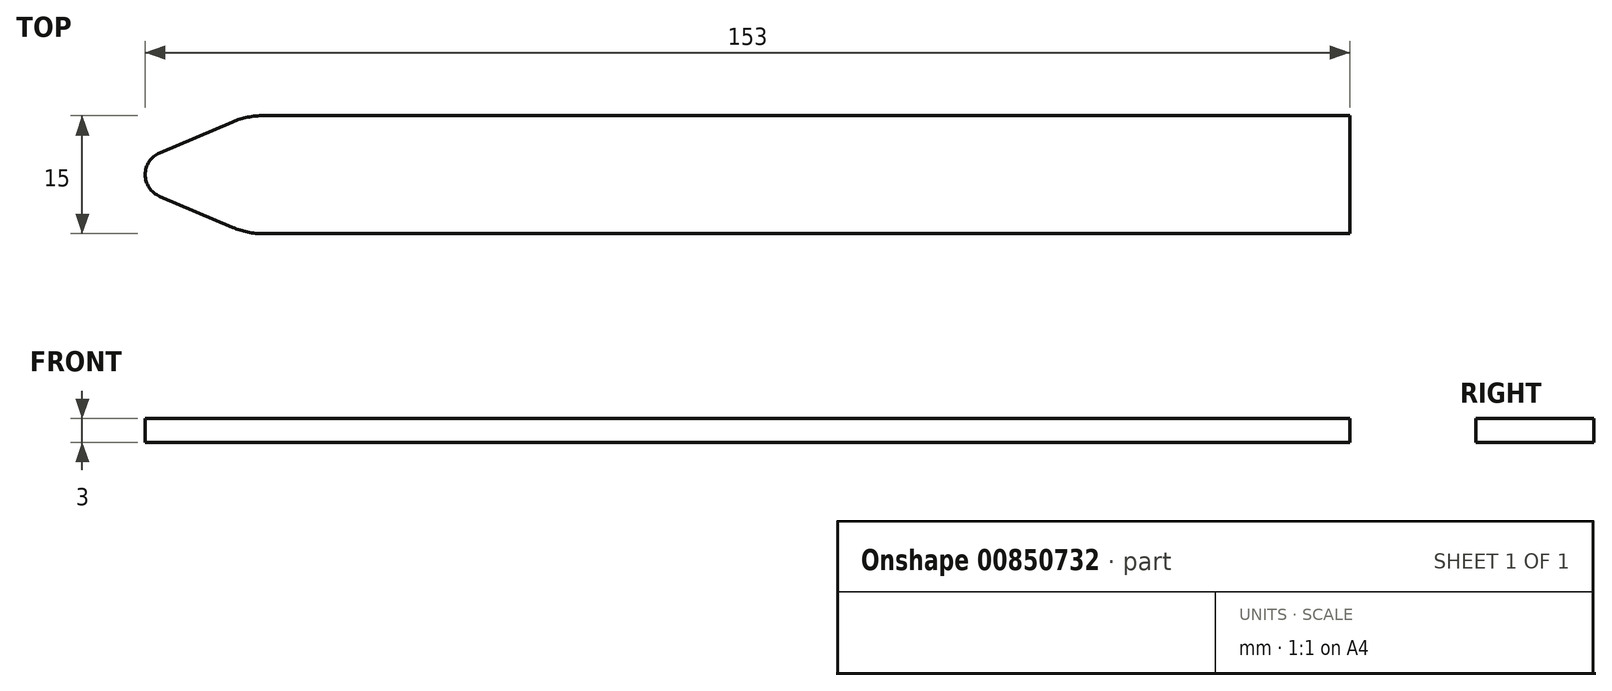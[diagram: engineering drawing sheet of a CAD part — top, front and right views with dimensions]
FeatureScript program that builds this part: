
annotation { "Feature Type Name" : "Feature", "Feature Type Description" : "" }
export const myFeature = defineFeature(function(context is Context, id is Id, definition is map)
    precondition{}
    {
        {
            var Q0;
            Q0=qCreatedBy(makeId("Top.planeOp"),FACE);
            var sketch = newSketch(context, id + "F0", { "sketchPlane" : qUnion([Q0])});
            skLineSegment(sketch, "E0", {"start": v(0, 0) * mm, "end": v(0, 7.5) * mm});
            skLineSegment(sketch, "E1", {"start": v(0, 7.5) * mm, "end": v(-138, 7.5) * mm});
            skLineSegment(sketch, "E2.MirrorCS", {"start": v(0, -7.5) * mm, "end": v(-138, -7.5) * mm});
            skLineSegment(sketch, "E3.MirrorCS", {"start": v(0, 0) * mm, "end": v(0, -7.5) * mm});
            skArc(sketch, "E4", {"start": v(-151.17, 2.76) * mm, "mid": v(-153, 0) * mm, "end": v(-151.17, -2.76) * mm});
            skLineSegment(sketch, "E5", {"start": v(-141.92, 6.7) * mm, "end": v(-151.17, 2.76) * mm});
            skArc(sketch, "E6.filletArc", {"start": v(-138, 7.5) * mm, "mid": v(-140, 7.3) * mm, "end": v(-141.92, 6.7) * mm});
            skArc(sketch, "E7.MirrorCS", {"start": v(-138, -7.5) * mm, "mid": v(-140, -7.3) * mm, "end": v(-141.92, -6.7) * mm});
            skLineSegment(sketch, "E8.MirrorCS", {"start": v(-141.92, -6.7) * mm, "end": v(-151.17, -2.76) * mm});
            skSolve(sketch);
        }
        {
            var Q0;
            Q0=makeQuery(id+"F0.imprint","IMPRINT",FACE,{"disambiguationData":[TD([[makeQuery(id+"F0.imprint","IMPRINT",EDGE,{"derivedFrom":sQuery(id+"F0.wireOp",EDGE,"E0")}),1.0]])]});
            extrude(context, id + "F1", {"entities" : qUnion([Q0]), "depth" : 3 * mm, "offsetDistance" : 25 * mm});
        }
    });
